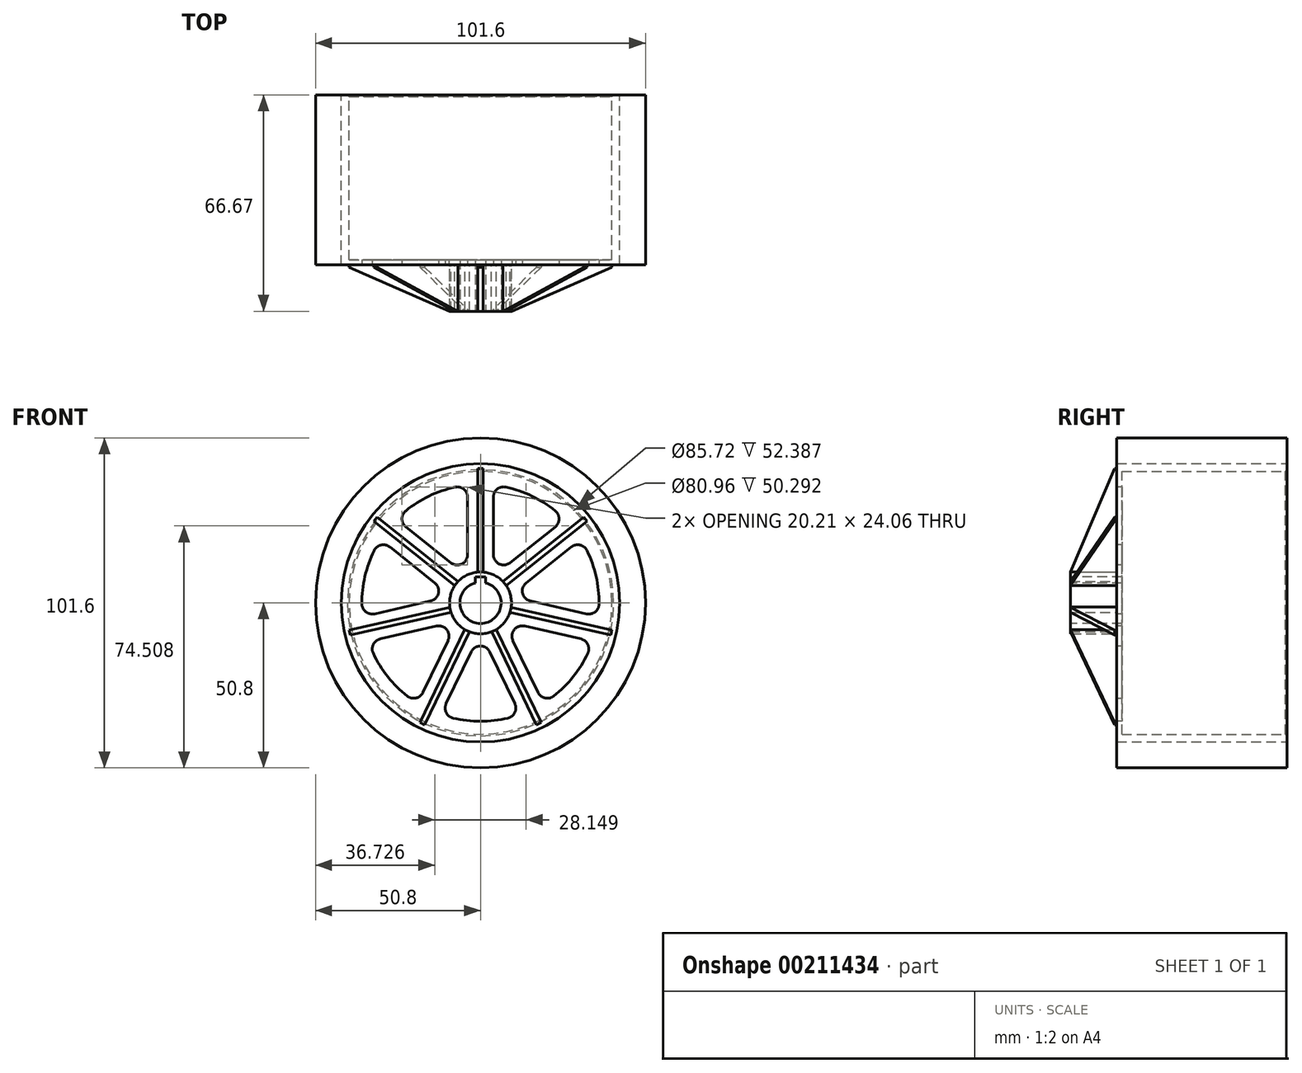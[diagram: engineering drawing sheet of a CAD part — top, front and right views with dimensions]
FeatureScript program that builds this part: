
annotation { "Feature Type Name" : "Feature", "Feature Type Description" : "" }
export const myFeature = defineFeature(function(context is Context, id is Id, definition is map)
    precondition{}
    {
        {
            var Q0;
            Q0=qCreatedBy(makeId("Front.planeOp"),FACE);
            var sketch = newSketch(context, id + "F0", { "sketchPlane" : qUnion([Q0])});
            skCircle(sketch, "E0", {"center": v(0, 0) * mm, "radius": 40.48 * mm});
            skCircle(sketch, "E1", {"center": v(0, 0) * mm, "radius": 42.86 * mm});
            skSolve(sketch);
        }
        {
            var Q0;
            Q0 = qSketchRegion(id + "F0", true);
            extrude(context, id + "F1", {"entities" : qUnion([Q0]), "depth" : 50.8 * mm});
        }
        {
            var Q0;
            Q0=makeQuery(id+"F1.opExtrude","CAP_FACE",FACE,{"disambiguationData":[OSD([sQuery(id+"F0.wireOp",EDGE,"E0"),sQuery(id+"F0.wireOp",EDGE,"E1")])],"isStart":false});
            var sketch = newSketch(context, id + "F2", { "sketchPlane" : qUnion([Q0])});
            skCircle(sketch, "E2.0", {"center": v(0, 0) * mm, "radius": 42.86 * mm});
            skSolve(sketch);
        }
        {
            var Q0;
            Q0 = qSketchRegion(id + "F2", true);
            extrude(context, id + "F3", {"entities" : qUnion([Q0]), "operationType" : NewBodyOperationType.ADD, "depth" : 1.59 * mm});
        }
        {
            var Q0;
            Q0=makeQuery(id+"F3.opExtrude","CAP_FACE",FACE,{"disambiguationData":[OSD([sQuery(id+"F2.wireOp",EDGE,"E2.0")])],"isStart":false});
            var sketch = newSketch(context, id + "F4", { "sketchPlane" : qUnion([Q0])});
            skCircle(sketch, "E3", {"center": v(0, 0) * mm, "radius": 9.53 * mm});
            skSolve(sketch);
        }
        {
            var Q0;
            Q0 = qSketchRegion(id + "F4", true);
            extrude(context, id + "F5", {"entities" : qUnion([Q0]), "operationType" : NewBodyOperationType.ADD, "depth" : 14.29 * mm});
        }
        {
            var Q0;
            Q0=qCreatedBy(makeId("Right.planeOp"),FACE);
            var sketch = newSketch(context, id + "F6", { "sketchPlane" : qUnion([Q0])});
            skLineSegment(sketch, "E4.0", {"start": v(-52.39, 4.5) * mm, "end": v(-52.39, 41.34) * mm});
            skLineSegment(sketch, "E5.0", {"start": v(-66.68, 4.5) * mm, "end": v(-66.68, 9.53) * mm});
            skPoint(sketch, "E6.orphan", {"position": v(-52.39, -42.86) * mm});
            skLineSegment(sketch, "E7", {"start": v(-66.68, 4.5) * mm, "end": v(-52.39, 4.5) * mm});
            skLineSegment(sketch, "E8", {"start": v(-53.04, 41.34) * mm, "end": v(-66.68, 9.52) * mm});
            skLineSegment(sketch, "E9", {"start": v(-52.39, 41.34) * mm, "end": v(-53.04, 41.34) * mm});
            skPoint(sketch, "E10.orphan", {"position": v(-52.39, 42.86) * mm});
            skLineSegment(sketch, "E11", {"start": v(-98.66, 0) * mm, "end": v(17.38, 0) * mm, "construction": true});
            skSolve(sketch);
        }
        {
            var Q0;
            Q0 = qSketchRegion(id + "F6", true);
            extrude(context, id + "F7", {"entities" : qUnion([Q0]), "endBound" : BoundingType.SYMMETRIC, "depth" : 1.59 * mm});
        }
        {
            var Q0;
            Q0=makeQuery(id+"F7.opExtrude","SWEPT_BODY",BODY,{"disambiguationData":[OSD([sQuery(id+"F6.wireOp",EDGE,"E4.0"),sQuery(id+"F6.wireOp",EDGE,"E5.0"),sQuery(id+"F6.wireOp",EDGE,"E7"),sQuery(id+"F6.wireOp",EDGE,"E8"),sQuery(id+"F6.wireOp",EDGE,"E9")])]});
            var Q1;
            Q1=sQuery(id+"F6.wireOp",EDGE,"E11");
            circularPattern(context, id + "F8", {"operationType" : NewBodyOperationType.ADD, "entities" : qUnion([Q0]), "axis" : qUnion([Q1]), "angle" : 360 * degree, "instanceCount" : 7, "equalSpace" : true});
        }
        {
            var Q0;
            {var subQ0=makeQuery(id+"F7.opExtrude","SWEPT_FACE",FACE,{"disambiguationData":[OSD([sQuery(id+"F6.wireOp",EDGE,"E5.0")])]});Q0=makeQuery(id+"F8.boolean.opBoolean","MERGE",FACE,{"derivedFrom":[makeQuery(id+"F5.opExtrude","CAP_FACE",FACE,{"disambiguationData":[OSD([sQuery(id+"F4.wireOp",EDGE,"E3")])],"isStart":false}),subQ0,makeQuery(id+"F8.opPattern","COPY",FACE,{"derivedFrom":subQ0,"instanceName":"1"}),makeQuery(id+"F8.opPattern","COPY",FACE,{"derivedFrom":subQ0,"instanceName":"2"}),makeQuery(id+"F8.opPattern","COPY",FACE,{"derivedFrom":subQ0,"instanceName":"3"}),makeQuery(id+"F8.opPattern","COPY",FACE,{"derivedFrom":subQ0,"instanceName":"4"}),makeQuery(id+"F8.opPattern","COPY",FACE,{"derivedFrom":subQ0,"instanceName":"5"}),makeQuery(id+"F8.opPattern","COPY",FACE,{"derivedFrom":subQ0,"instanceName":"6"})]});}
            var sketch = newSketch(context, id + "F9", { "sketchPlane" : qUnion([Q0])});
            skArc(sketch, "E12", {"start": v(-1.59, 6.15) * mm, "mid": v(0, -6.35) * mm, "end": v(1.59, 6.15) * mm});
            skLineSegment(sketch, "E13.bottom", {"start": v(-1.59, 7.94) * mm, "end": v(1.59, 7.94) * mm});
            skLineSegment(sketch, "E13.top", {"start": v(-1.59, 4.76) * mm, "end": v(1.59, 4.76) * mm, "construction": true});
            skLineSegment(sketch, "E13.left", {"start": v(-1.59, 7.94) * mm, "end": v(-1.59, 6.15) * mm});
            skLineSegment(sketch, "E13.right", {"start": v(1.59, 7.94) * mm, "end": v(1.59, 6.15) * mm});
            skLineSegment(sketch, "E14", {"start": v(-1.59, 7.94) * mm, "end": v(1.59, 4.76) * mm, "construction": true});
            skPoint(sketch, "E15", {"position": v(0, 6.35) * mm});
            skLineSegment(sketch, "E16", {"start": v(0, 0) * mm, "end": v(0, 16.67) * mm, "construction": true});
            skLineSegment(sketch, "E17", {"start": v(1.59, 6.15) * mm, "end": v(1.59, 4.76) * mm, "construction": true});
            skLineSegment(sketch, "E18", {"start": v(-1.59, 6.15) * mm, "end": v(-1.59, 4.76) * mm, "construction": true});
            skSolve(sketch);
        }
        {
            var Q0;
            Q0 = qSketchRegion(id + "F9", true);
            extrude(context, id + "F10", {"entities" : qUnion([Q0]), "operationType" : NewBodyOperationType.REMOVE, "endBound" : BoundingType.THROUGH_ALL, "oppositeDirection" : true, "depth" : 25.4 * mm});
        }
        {
            var Q0;
            Q0=qCreatedBy(makeId("Front.planeOp"),FACE);
            var sketch = newSketch(context, id + "F11", { "sketchPlane" : qUnion([Q0])});
            skCircle(sketch, "E19", {"center": v(0, 0) * mm, "radius": 42.86 * mm});
            skCircle(sketch, "E20", {"center": v(0, 0) * mm, "radius": 50.8 * mm});
            skSolve(sketch);
        }
        {
            var Q0;
            Q0 = qSketchRegion(id + "F11", true);
            var Q1;
            Q1=makeQuery(id+"F3.opExtrude","CAP_FACE",FACE,{"disambiguationData":[OSD([sQuery(id+"F2.wireOp",EDGE,"E2.0")])],"isStart":false});
            extrude(context, id + "F12", {"entities" : qUnion([Q0]), "endBound" : BoundingType.UP_TO_SURFACE, "endBoundEntityFace" : qUnion([Q1]), "depth" : 76.2 * mm});
        }
        {
            var Q0;
            Q0=makeQuery(id+"F3.opExtrude","CAP_FACE",FACE,{"disambiguationData":[OSD([sQuery(id+"F2.wireOp",EDGE,"E2.0")])],"isStart":false});
            var sketch = newSketch(context, id + "F13", { "sketchPlane" : qUnion([Q0])});
            skLineSegment(sketch, "E21", {"start": v(2.86, -15.09) * mm, "end": v(10.55, -31.06) * mm});
            skLineSegment(sketch, "E22", {"start": v(-10.55, -31.06) * mm, "end": v(-2.86, -15.09) * mm});
            skArc(sketch, "E23.0", {"start": v(-8.42, -35.53) * mm, "mid": v(0, -36.51) * mm, "end": v(8.42, -35.53) * mm});
            skPoint(sketch, "E24.visualSharp", {"position": v(12.17, -34.42) * mm});
            skArc(sketch, "E24.filletArc", {"start": v(8.42, -35.53) * mm, "mid": v(10.56, -33.8) * mm, "end": v(10.55, -31.06) * mm});
            skPoint(sketch, "E25.visualSharp", {"position": v(-12.17, -34.42) * mm});
            skArc(sketch, "E25.filletArc", {"start": v(-10.55, -31.06) * mm, "mid": v(-10.56, -33.8) * mm, "end": v(-8.42, -35.53) * mm});
            skPoint(sketch, "E26.visualSharp", {"position": v(0, -9.15) * mm});
            skArc(sketch, "E26.filletArc", {"start": v(2.86, -15.09) * mm, "mid": v(0, -13.29) * mm, "end": v(-2.86, -15.09) * mm});
            skLineSegment(sketch, "E27.1.0", {"start": v(13.58, -7.17) * mm, "end": v(30.86, -11.12) * mm});
            skArc(sketch, "E27.1.1", {"start": v(13.58, -7.17) * mm, "mid": v(10.4, -8.29) * mm, "end": v(10.01, -11.64) * mm});
            skLineSegment(sketch, "E27.1.2", {"start": v(17.7, -27.62) * mm, "end": v(10.01, -11.64) * mm});
            skArc(sketch, "E27.1.3", {"start": v(17.7, -27.62) * mm, "mid": v(19.85, -29.33) * mm, "end": v(22.52, -28.74) * mm});
            skArc(sketch, "E27.1.4", {"start": v(22.52, -28.74) * mm, "mid": v(28.55, -22.77) * mm, "end": v(33.03, -15.56) * mm});
            skArc(sketch, "E27.1.5", {"start": v(33.03, -15.56) * mm, "mid": v(33.01, -12.82) * mm, "end": v(30.86, -11.12) * mm});
            skLineSegment(sketch, "E27.2.0", {"start": v(14.07, 6.15) * mm, "end": v(27.93, 17.2) * mm});
            skArc(sketch, "E27.2.1", {"start": v(14.07, 6.15) * mm, "mid": v(12.96, 2.96) * mm, "end": v(15.35, 0.57) * mm});
            skLineSegment(sketch, "E27.2.2", {"start": v(32.63, -3.38) * mm, "end": v(15.35, 0.57) * mm});
            skArc(sketch, "E27.2.3", {"start": v(32.63, -3.38) * mm, "mid": v(35.3, -2.77) * mm, "end": v(36.51, -0.3) * mm});
            skArc(sketch, "E27.2.4", {"start": v(36.51, -0.3) * mm, "mid": v(35.6, 8.12) * mm, "end": v(32.76, 16.12) * mm});
            skArc(sketch, "E27.2.5", {"start": v(32.76, 16.12) * mm, "mid": v(30.6, 17.82) * mm, "end": v(27.93, 17.2) * mm});
            skLineSegment(sketch, "E27.3.0", {"start": v(3.97, 14.83) * mm, "end": v(3.97, 32.56) * mm});
            skArc(sketch, "E27.3.1", {"start": v(3.97, 14.83) * mm, "mid": v(5.77, 11.97) * mm, "end": v(9.12, 12.35) * mm});
            skLineSegment(sketch, "E27.3.2", {"start": v(22.98, 23.4) * mm, "end": v(9.12, 12.35) * mm});
            skArc(sketch, "E27.3.3", {"start": v(22.98, 23.4) * mm, "mid": v(24.18, 25.87) * mm, "end": v(23, 28.35) * mm});
            skArc(sketch, "E27.3.4", {"start": v(23, 28.35) * mm, "mid": v(15.84, 32.9) * mm, "end": v(7.82, 35.66) * mm});
            skArc(sketch, "E27.3.5", {"start": v(7.82, 35.66) * mm, "mid": v(5.15, 35.04) * mm, "end": v(3.97, 32.56) * mm});
            skLineSegment(sketch, "E27.4.0", {"start": v(-9.12, 12.35) * mm, "end": v(-22.98, 23.4) * mm});
            skArc(sketch, "E27.4.1", {"start": v(-9.12, 12.35) * mm, "mid": v(-5.77, 11.97) * mm, "end": v(-3.97, 14.83) * mm});
            skLineSegment(sketch, "E27.4.2", {"start": v(-3.97, 32.56) * mm, "end": v(-3.97, 14.83) * mm});
            skArc(sketch, "E27.4.3", {"start": v(-3.97, 32.56) * mm, "mid": v(-5.15, 35.04) * mm, "end": v(-7.82, 35.66) * mm});
            skArc(sketch, "E27.4.4", {"start": v(-7.82, 35.66) * mm, "mid": v(-15.84, 32.9) * mm, "end": v(-23, 28.35) * mm});
            skArc(sketch, "E27.4.5", {"start": v(-23, 28.35) * mm, "mid": v(-24.18, 25.87) * mm, "end": v(-22.98, 23.4) * mm});
            skLineSegment(sketch, "E27.5.0", {"start": v(-15.35, 0.57) * mm, "end": v(-32.63, -3.38) * mm});
            skArc(sketch, "E27.5.1", {"start": v(-15.35, 0.57) * mm, "mid": v(-12.96, 2.96) * mm, "end": v(-14.07, 6.15) * mm});
            skLineSegment(sketch, "E27.5.2", {"start": v(-27.93, 17.2) * mm, "end": v(-14.07, 6.15) * mm});
            skArc(sketch, "E27.5.3", {"start": v(-27.93, 17.2) * mm, "mid": v(-30.6, 17.82) * mm, "end": v(-32.76, 16.12) * mm});
            skArc(sketch, "E27.5.4", {"start": v(-32.76, 16.12) * mm, "mid": v(-35.6, 8.12) * mm, "end": v(-36.51, -0.3) * mm});
            skArc(sketch, "E27.5.5", {"start": v(-36.51, -0.3) * mm, "mid": v(-35.3, -2.77) * mm, "end": v(-32.63, -3.38) * mm});
            skLineSegment(sketch, "E27.6.0", {"start": v(-10.01, -11.64) * mm, "end": v(-17.7, -27.62) * mm});
            skArc(sketch, "E27.6.1", {"start": v(-10.01, -11.64) * mm, "mid": v(-10.4, -8.29) * mm, "end": v(-13.58, -7.17) * mm});
            skLineSegment(sketch, "E27.6.2", {"start": v(-30.86, -11.12) * mm, "end": v(-13.58, -7.17) * mm});
            skArc(sketch, "E27.6.3", {"start": v(-30.86, -11.12) * mm, "mid": v(-33.01, -12.82) * mm, "end": v(-33.03, -15.56) * mm});
            skArc(sketch, "E27.6.4", {"start": v(-33.03, -15.56) * mm, "mid": v(-28.55, -22.77) * mm, "end": v(-22.52, -28.74) * mm});
            skArc(sketch, "E27.6.5", {"start": v(-22.52, -28.74) * mm, "mid": v(-19.85, -29.33) * mm, "end": v(-17.7, -27.62) * mm});
            skSolve(sketch);
        }
        {
            var Q0;
            Q0 = qSketchRegion(id + "F13", true);
            extrude(context, id + "F14", {"entities" : qUnion([Q0]), "operationType" : NewBodyOperationType.REMOVE, "endBound" : BoundingType.UP_TO_NEXT, "oppositeDirection" : true, "depth" : 25.4 * mm});
        }
        {
            var Q0;
            Q0=makeQuery(id+"F1.opExtrude","CAP_EDGE",EDGE,{"disambiguationData":[OSD([sQuery(id+"F0.wireOp",EDGE,"E0")])],"isStart":true});
            chamfer(context, id + "F15", {"entities" : qUnion([Q0]), "width" : 0.5 * mm, "tangentPropagation" : true});
        }
    });
